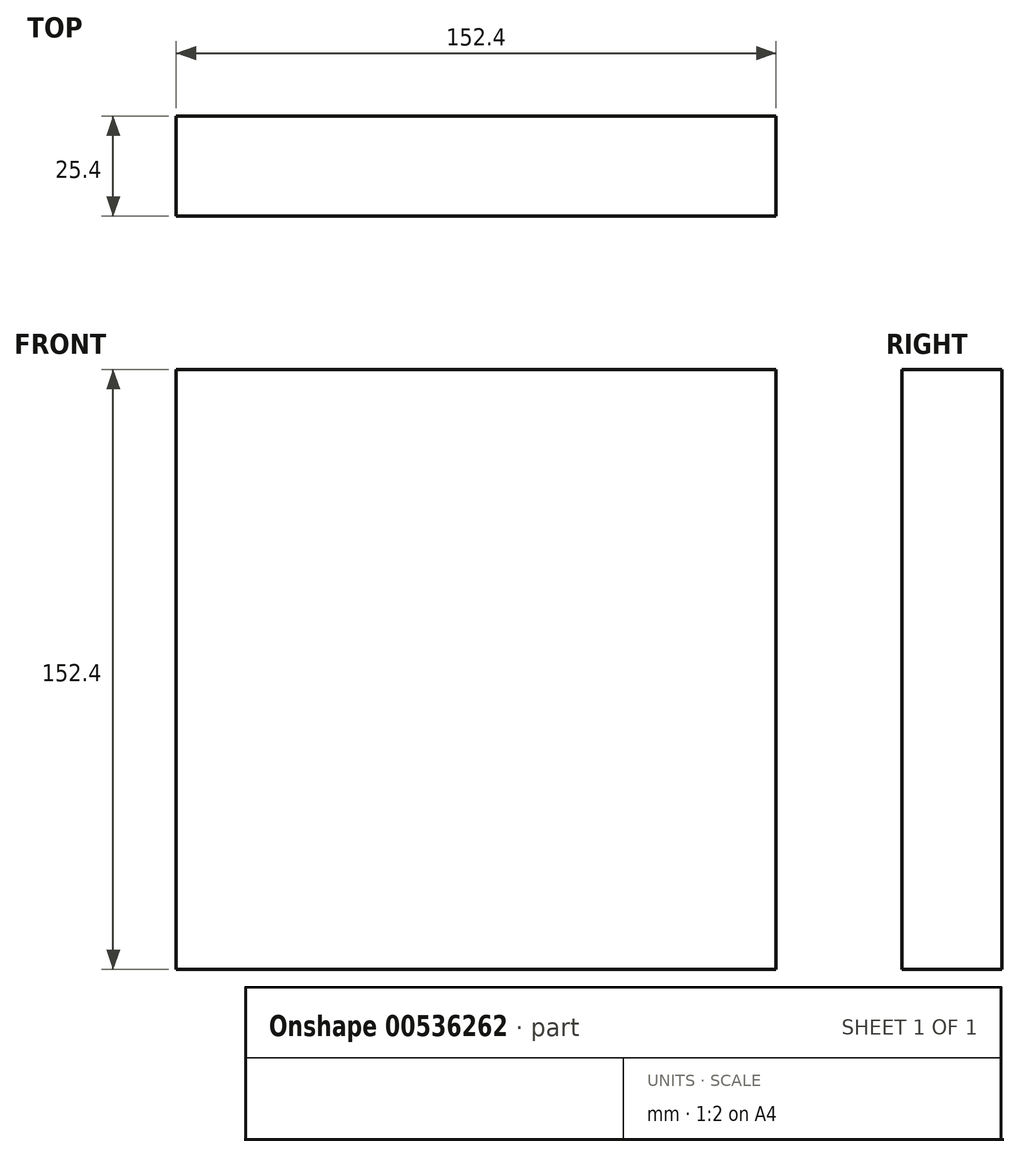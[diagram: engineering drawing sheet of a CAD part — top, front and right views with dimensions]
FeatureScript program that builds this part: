
annotation { "Feature Type Name" : "Feature", "Feature Type Description" : "" }
export const myFeature = defineFeature(function(context is Context, id is Id, definition is map)
    precondition{}
    {
        {
            var Q0;
            Q0=qCreatedBy(makeId("Front.planeOp"),FACE);
            var sketch = newSketch(context, id + "F0", { "sketchPlane" : qUnion([Q0])});
            skLineSegment(sketch, "E0.bottom", {"start": v(-76.11, 75.88) * mm, "end": v(76.29, 75.88) * mm});
            skLineSegment(sketch, "E0.top", {"start": v(-76.11, -76.52) * mm, "end": v(76.29, -76.52) * mm});
            skLineSegment(sketch, "E0.left", {"start": v(-76.11, 75.88) * mm, "end": v(-76.11, -76.52) * mm});
            skLineSegment(sketch, "E0.right", {"start": v(76.29, 75.88) * mm, "end": v(76.29, -76.52) * mm});
            skSolve(sketch);
        }
        {
            var Q0;
            Q0=makeQuery(id+"F0.imprint","IMPRINT",FACE,{"disambiguationData":[TD([[makeQuery(id+"F0.imprint","IMPRINT",EDGE,{"derivedFrom":sQuery(id+"F0.wireOp",EDGE,"E0.bottom")}),-1.0]])]});
            extrude(context, id + "F1", {"entities" : qUnion([Q0]), "depth" : 25.4 * mm, "offsetDistance" : 25.4 * mm});
        }
    });
